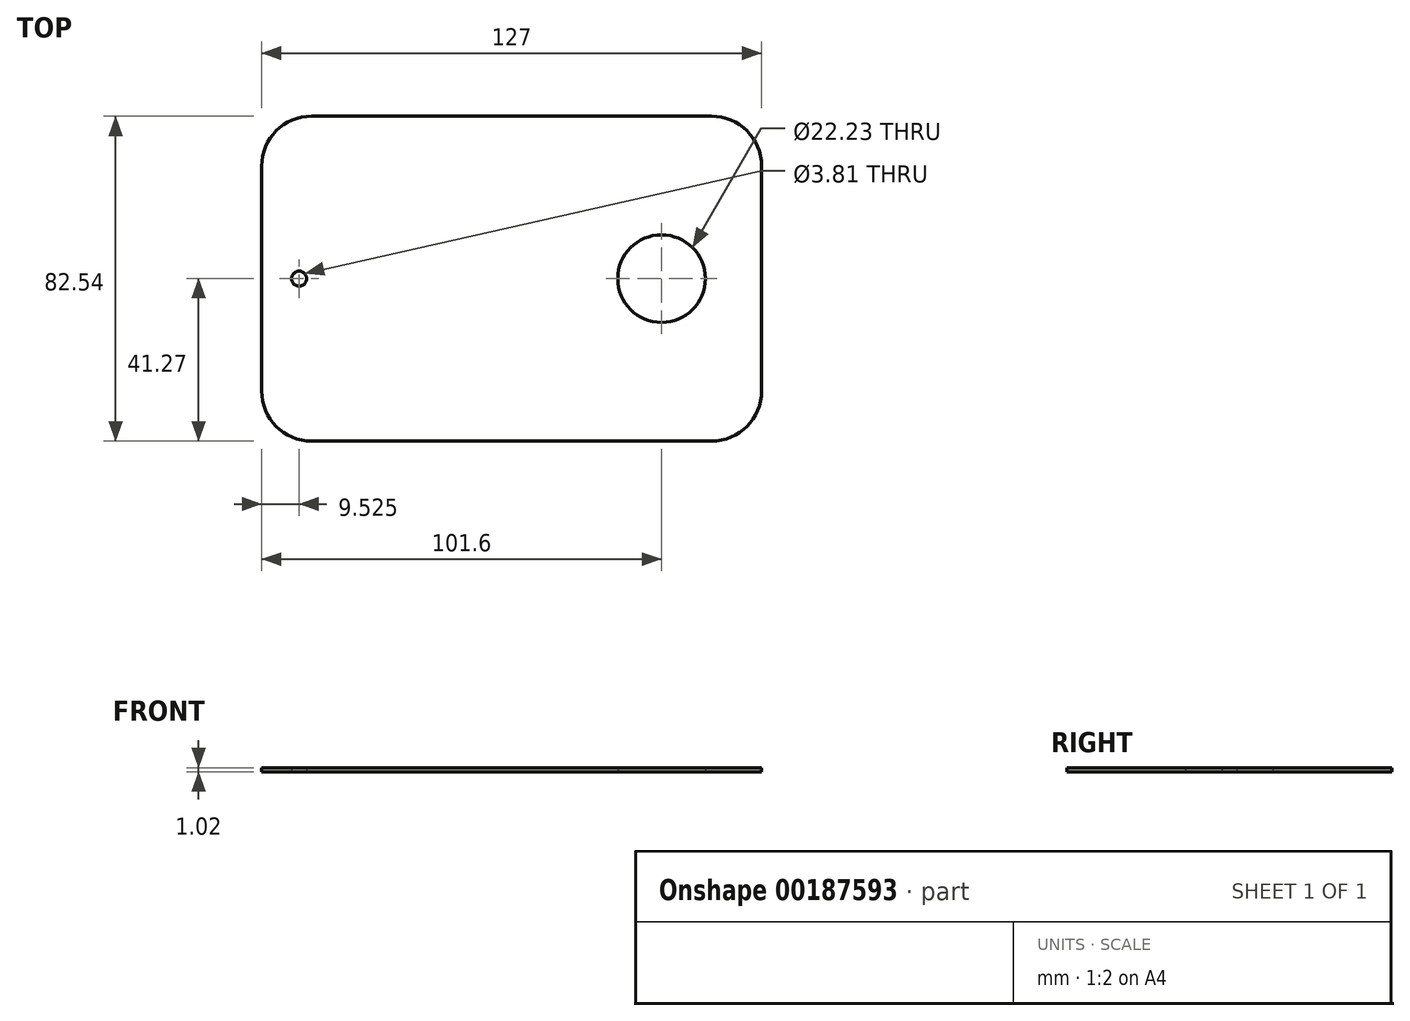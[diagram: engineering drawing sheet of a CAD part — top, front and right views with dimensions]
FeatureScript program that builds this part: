
annotation { "Feature Type Name" : "Feature", "Feature Type Description" : "" }
export const myFeature = defineFeature(function(context is Context, id is Id, definition is map)
    precondition{}
    {
        {
            var Q0;
            Q0=qCreatedBy(makeId("Top.planeOp"),FACE);
            var sketch = newSketch(context, id + "F0", { "sketchPlane" : qUnion([Q0])});
            skCircle(sketch, "E0", {"center": v(0, 0) * mm, "radius": 11.11 * mm});
            skLineSegment(sketch, "E1.bottom", {"start": v(-88.9, 41.28) * mm, "end": v(12.7, 41.28) * mm});
            skLineSegment(sketch, "E1.top", {"start": v(-88.9, -41.28) * mm, "end": v(12.7, -41.28) * mm});
            skLineSegment(sketch, "E1.left", {"start": v(-101.6, 28.58) * mm, "end": v(-101.6, -28.58) * mm});
            skLineSegment(sketch, "E1.right", {"start": v(25.4, 28.58) * mm, "end": v(25.4, -28.57) * mm});
            skLineSegment(sketch, "E2", {"start": v(-25.4, 31.75) * mm, "end": v(-25.4, -31.75) * mm, "construction": true});
            skLineSegment(sketch, "E3", {"start": v(-54.2, 31.75) * mm, "end": v(-54.2, -31.75) * mm, "construction": true});
            skLineSegment(sketch, "E4", {"start": v(-82.55, 31.75) * mm, "end": v(-82.55, -31.75) * mm, "construction": true});
            skLineSegment(sketch, "E5", {"start": v(0, 0) * mm, "end": v(-152.4, 0) * mm, "construction": true});
            skPoint(sketch, "E6", {"position": v(-25.4, 0) * mm});
            skPoint(sketch, "E7", {"position": v(-54.2, 0) * mm});
            skPoint(sketch, "E8", {"position": v(-82.55, 0) * mm});
            skPoint(sketch, "E9", {"position": v(25.4, 0) * mm});
            skCircle(sketch, "E10", {"center": v(-92.08, 0) * mm, "radius": 1.9 * mm});
            skPoint(sketch, "E11.visualSharp", {"position": v(-101.6, 41.28) * mm});
            skArc(sketch, "E11.filletArc", {"start": v(-88.9, 41.28) * mm, "mid": v(-97.88, 37.56) * mm, "end": v(-101.6, 28.58) * mm});
            skPoint(sketch, "E12.visualSharp", {"position": v(25.4, 41.28) * mm});
            skArc(sketch, "E12.filletArc", {"start": v(25.4, 28.58) * mm, "mid": v(21.68, 37.56) * mm, "end": v(12.7, 41.28) * mm});
            skPoint(sketch, "E13.visualSharp", {"position": v(25.4, -41.28) * mm});
            skArc(sketch, "E13.filletArc", {"start": v(12.7, -41.27) * mm, "mid": v(21.68, -37.56) * mm, "end": v(25.4, -28.57) * mm});
            skPoint(sketch, "E14.visualSharp", {"position": v(-101.6, -41.28) * mm});
            skArc(sketch, "E14.filletArc", {"start": v(-101.6, -28.58) * mm, "mid": v(-97.88, -37.56) * mm, "end": v(-88.9, -41.28) * mm});
            skLineSegment(sketch, "E15", {"start": v(-54.2, -31.75) * mm, "end": v(-54.2, -127) * mm, "construction": true});
            skLineSegment(sketch, "E16", {"start": v(0, 0) * mm, "end": v(0, -127) * mm, "construction": true});
            skSolve(sketch);
        }
        {
            var Q0;
            Q0 = qSketchRegion(id + "F0", true);
            extrude(context, id + "F1", {"entities" : qUnion([Q0]), "depth" : 1.02 * mm});
        }
    });
